# Revit family: EKF_EE_КорпусВРУ-1мЦельносворной_IP31_PROxima
name_source: partatom
category: Электрооборудование
units: mm (PartAtom-declared; Revit-internal decimal feet)

## family parameters
Всегда вертикально = Нет
На основе рабочей плоскости = Да
Общий = Да
При загрузке вырезать с полостями = Нет
Размер круглого соединителя = Использовать диаметр
Тип детали = Силовой щит
Точка расчета площади = Нет

## types (1)
- Корпус ВРУ-1м IP31 цельносв. с боковыми панелями и задней стенкой (1700х800х450) EKF PROxima
    ADSK_Единица измерения = шт.
    ADSK_Завод-изготовитель = EKF
    ADSK_Код изделия = mb05-01-00m
    ADSK_Количество = 1
    ADSK_Марка = Корпус
    ADSK_Масса = 66
    ADSK_Материал = RAL 7035_Сталь
    ADSK_Наименование = Корпус ВРУ-1м IP31 цельносв. с боковыми панелями и задней стенкой (1700х800х450) EKF PROxima
    ADSK_Обозначение = Корпус
    ADSK_Размер_Высота = 1700 мм
    ADSK_Размер_Глубина = 450 мм
    ADSK_Размер_Ширина = 800 мм
    t = 20 мм
    Дверь_a = 755 мм
    Дверь_h = 1580 мм
    Изготовитель = EKF
    Отметка по умолчанию = 0 мм
    Рейка_Ширина = 419 мм
    РейкаПопереч_Шаг = 700 мм
    Рейки_Отступ = 26.5 мм
    Серия номенклатуры = PROxima
    Степень защиты IP = IP31
    ТВ = EKF_2
    Тип = 4 мм
    Тип установки = Напольный
